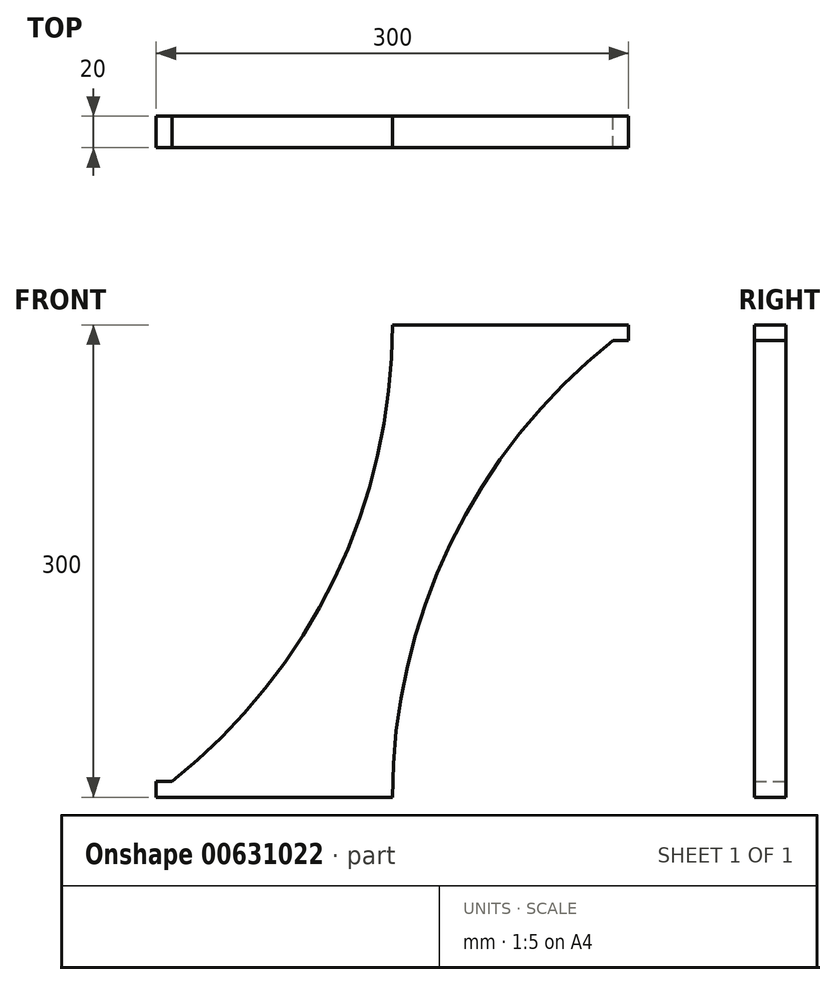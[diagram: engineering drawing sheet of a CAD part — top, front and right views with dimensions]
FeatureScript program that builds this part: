
annotation { "Feature Type Name" : "Feature", "Feature Type Description" : "" }
export const myFeature = defineFeature(function(context is Context, id is Id, definition is map)
    precondition{}
    {
        {
            var Q0;
            Q0=qCreatedBy(makeId("Front.planeOp"),FACE);
            var sketch = newSketch(context, id + "F0", { "sketchPlane" : qUnion([Q0])});
            skPoint(sketch, "E0.start.orphan", {"position": v(682.2, 671.17) * mm});
            skPoint(sketch, "E1.end.orphan", {"position": v(44.74, 0) * mm});
            skPoint(sketch, "E1.start.orphan", {"position": v(637.46, 671.17) * mm});
            skPoint(sketch, "E2.end.orphan", {"position": v(592.72, 671.17) * mm});
            skPoint(sketch, "E3.orphan", {"position": v(89.49, 0) * mm});
            skPoint(sketch, "E4.end.orphan", {"position": v(0, 0) * mm});
            skLineSegment(sketch, "E5", {"start": v(0, 0) * mm, "end": v(150, 0) * mm});
            skPoint(sketch, "E6.start.orphan", {"position": v(156.16, 0) * mm});
            skPoint(sketch, "E7.end.orphan", {"position": v(156.16, -19.62) * mm});
            skLineSegment(sketch, "E8", {"start": v(150, 0) * mm, "end": v(150, 300) * mm});
            skLineSegment(sketch, "E9", {"start": v(150, 300) * mm, "end": v(300, 300) * mm});
            skLineSegment(sketch, "E10", {"start": v(0, 0) * mm, "end": v(0, 10) * mm});
            skLineSegment(sketch, "E11", {"start": v(0, 10) * mm, "end": v(10, 10) * mm});
            skArc(sketch, "E12", {"start": v(10, 10) * mm, "mid": v(113.17, 138.99) * mm, "end": v(150, 300) * mm});
            skLineSegment(sketch, "E13", {"start": v(300, 300) * mm, "end": v(300, 290) * mm});
            skLineSegment(sketch, "E14", {"start": v(300, 290) * mm, "end": v(290, 290) * mm});
            skArc(sketch, "E15", {"start": v(290, 290) * mm, "mid": v(186.83, 161.01) * mm, "end": v(150, 0) * mm});
            skSolve(sketch);
        }
        {
            var Q0;
            Q0 = qSketchRegion(id + "F0", true);
            extrude(context, id + "F1", {"entities" : qUnion([Q0]), "depth" : 20 * mm, "offsetDistance" : 25 * mm});
        }
    });
